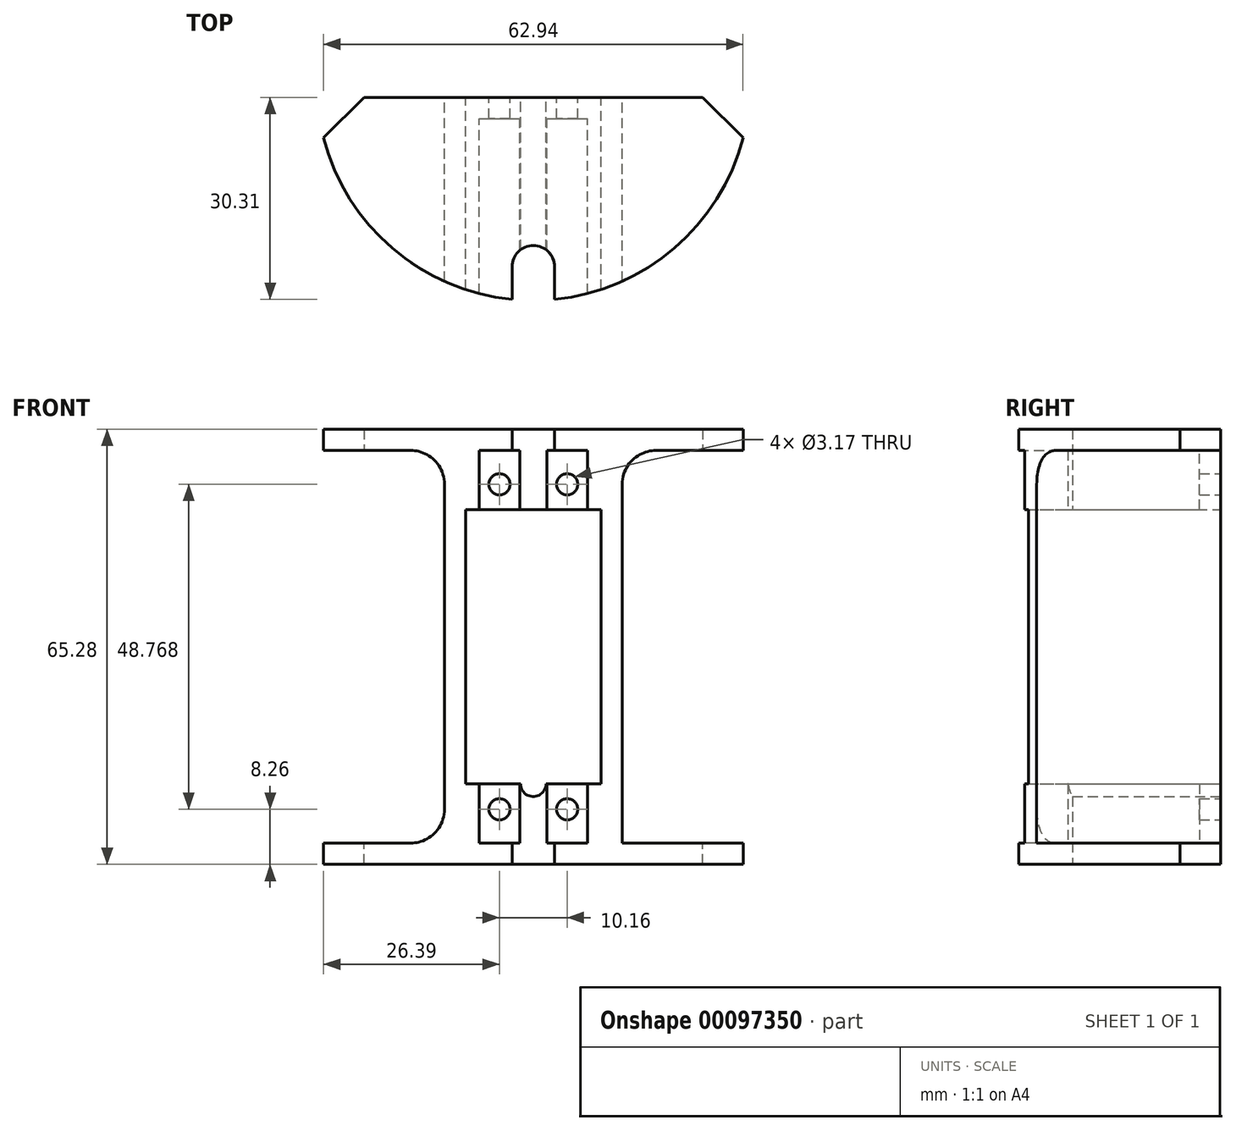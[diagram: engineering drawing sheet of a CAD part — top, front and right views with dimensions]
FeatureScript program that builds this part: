
annotation { "Feature Type Name" : "Feature", "Feature Type Description" : "" }
export const myFeature = defineFeature(function(context is Context, id is Id, definition is map)
    precondition{}
    {
        {
            var Q0;
            Q0=qCreatedBy(makeId("Front.planeOp"),FACE);
            var sketch = newSketch(context, id + "F0", { "sketchPlane" : qUnion([Q0])});
            skLineSegment(sketch, "E0", {"start": v(0, 0) * mm, "end": v(0, 41.15) * mm});
            skLineSegment(sketch, "E1", {"start": v(0, 41.15) * mm, "end": v(-20.32, 41.15) * mm});
            skLineSegment(sketch, "E2", {"start": v(-20.32, 41.15) * mm, "end": v(-20.32, 0) * mm});
            skLineSegment(sketch, "E3", {"start": v(-20.32, 0) * mm, "end": v(-12.07, 0) * mm});
            skLineSegment(sketch, "E4.0", {"start": v(-23.5, 50.04) * mm, "end": v(-23.5, -8.9) * mm});
            skLineSegment(sketch, "E5.0", {"start": v(3.17, 50.04) * mm, "end": v(-23.5, 50.04) * mm});
            skLineSegment(sketch, "E6.0", {"start": v(3.18, -8.9) * mm, "end": v(3.18, 50.04) * mm});
            skLineSegment(sketch, "E7.0", {"start": v(-23.5, -8.9) * mm, "end": v(3.18, -8.9) * mm});
            skLineSegment(sketch, "E8", {"start": v(-23.5, 44.96) * mm, "end": v(3.18, 44.96) * mm, "construction": true});
            skLineSegment(sketch, "E9", {"start": v(-23.5, 20.57) * mm, "end": v(3.18, 20.57) * mm, "construction": true});
            skLineSegment(sketch, "E10", {"start": v(-10.16, 50.04) * mm, "end": v(-10.16, -8.9) * mm, "construction": true});
            skLineSegment(sketch, "E11.MirrorCS", {"start": v(-23.5, -3.81) * mm, "end": v(3.18, -3.8) * mm, "construction": true});
            skCircle(sketch, "E12", {"center": v(-5.08, 44.96) * mm, "radius": 1.59 * mm});
            skCircle(sketch, "E13.MirrorC", {"center": v(-15.24, 44.96) * mm, "radius": 1.59 * mm});
            skCircle(sketch, "E14.MirrorC", {"center": v(-15.24, -3.81) * mm, "radius": 1.59 * mm});
            skCircle(sketch, "E15.MirrorC", {"center": v(-5.08, -3.81) * mm, "radius": 1.59 * mm});
            skArc(sketch, "E16", {"start": v(-12.07, 0) * mm, "mid": v(-10.16, -1.9) * mm, "end": v(-8.26, 0) * mm});
            skLineSegment(sketch, "E17.trimOffspring", {"start": v(-8.26, 0) * mm, "end": v(0, 0) * mm});
            skSolve(sketch);
        }
        {
            var Q0;
            Q0=makeQuery(id+"F0.imprint","IMPRINT",FACE,{"disambiguationData":[TD([[makeQuery(id+"F0.imprint","IMPRINT",EDGE,{"derivedFrom":sQuery(id+"F0.wireOp",EDGE,"E0")}),-1.0]])]});
            extrude(context, id + "F1", {"entities" : qUnion([Q0]), "depth" : 3.17 * mm});
        }
        {
            var Q0;
            Q0=makeQuery(id+"F1.opExtrude","CAP_FACE",FACE,{"disambiguationData":[OSD([sQuery(id+"F0.wireOp",EDGE,"E0"),sQuery(id+"F0.wireOp",EDGE,"E1"),sQuery(id+"F0.wireOp",EDGE,"E2"),sQuery(id+"F0.wireOp",EDGE,"E3"),sQuery(id+"F0.wireOp",EDGE,"E4.0"),sQuery(id+"F0.wireOp",EDGE,"E5.0"),sQuery(id+"F0.wireOp",EDGE,"E6.0"),sQuery(id+"F0.wireOp",EDGE,"E7.0"),sQuery(id+"F0.wireOp",EDGE,"E12"),sQuery(id+"F0.wireOp",EDGE,"E13.MirrorC"),sQuery(id+"F0.wireOp",EDGE,"E14.MirrorC"),sQuery(id+"F0.wireOp",EDGE,"E15.MirrorC")])],"isStart":false});
            var sketch = newSketch(context, id + "F2", { "sketchPlane" : qUnion([Q0])});
            skLineSegment(sketch, "E18", {"start": v(-2.03, 0) * mm, "end": v(-2.03, -8.9) * mm});
            skLineSegment(sketch, "E19", {"start": v(-2.03, 41.15) * mm, "end": v(-2.03, 50.04) * mm});
            skLineSegment(sketch, "E20", {"start": v(-10.16, -8.9) * mm, "end": v(-10.16, 50.04) * mm, "construction": true});
            skLineSegment(sketch, "E21.MirrorCS", {"start": v(-18.29, 0) * mm, "end": v(-18.29, -8.9) * mm});
            skLineSegment(sketch, "E22.MirrorCS", {"start": v(-18.29, 41.15) * mm, "end": v(-18.29, 50.04) * mm});
            skLineSegment(sketch, "E23", {"start": v(-8.13, 0) * mm, "end": v(-8.13, -8.9) * mm});
            skLineSegment(sketch, "E24", {"start": v(-8.13, 41.15) * mm, "end": v(-8.13, 50.04) * mm});
            skLineSegment(sketch, "E25.MirrorCS", {"start": v(-12.2, 0) * mm, "end": v(-12.2, -8.9) * mm});
            skLineSegment(sketch, "E26.MirrorCS", {"start": v(-12.2, 41.15) * mm, "end": v(-12.2, 50.04) * mm});
            skSolve(sketch);
        }
        {
            var Q0;
            {var subQ5=sQuery(id+"F2.wireOp",EDGE,"E18");Q0=makeQuery(id+"F2.imprint","IMPRINT",FACE,{"disambiguationData":[TD([[makeQuery(id+"F2.imprint","IMPRINT",EDGE,{"derivedFrom":subQ5}),1.0]])]});}
            var Q1;
            {var subQ0=sQuery(id+"F2.wireOp",EDGE,"E23");Q1=makeQuery(id+"F2.imprint","IMPRINT",FACE,{"disambiguationData":[TD([[makeQuery(id+"F2.imprint","IMPRINT",EDGE,{"derivedFrom":subQ0}),-1.0]])]});}
            var Q2;
            {var subQ2=sQuery(id+"F2.wireOp",EDGE,"E21.MirrorCS");Q2=makeQuery(id+"F2.imprint","IMPRINT",FACE,{"disambiguationData":[TD([[makeQuery(id+"F2.imprint","IMPRINT",EDGE,{"derivedFrom":subQ2}),-1.0]])]});}
            var Q3;
            {var subQ0=sQuery(id+"F2.wireOp",EDGE,"E24");Q3=makeQuery(id+"F2.imprint","IMPRINT",FACE,{"disambiguationData":[TD([[makeQuery(id+"F2.imprint","IMPRINT",EDGE,{"derivedFrom":subQ0}),1.0]])]});}
            extrude(context, id + "F3", {"entities" : qUnion([Q0, Q1, Q2, Q3]), "operationType" : NewBodyOperationType.ADD, "depth" : 38.1 * mm});
        }
        {
            var Q0;
            {var subQ0=sQuery(id+"F0.wireOp",EDGE,"E5.0");var subQ1=makeQuery(id+"F1.opExtrude","CAP_EDGE",EDGE,{"disambiguationData":[OSD([subQ0])],"isStart":false});Q0=makeQuery(id+"F3.boolean.opBoolean","MERGE",FACE,{"derivedFrom":[makeQuery(id+"F1.opExtrude","SWEPT_FACE",FACE,{"disambiguationData":[OSD([subQ0])]}),makeQuery(id+"F3.opExtrude","SWEPT_FACE",FACE,{"disambiguationData":[OSD([subQ0]),TDD([makeQuery(id+"F2.imprint","IMPRINT",EDGE,{"disambiguationData":[TD([[makeQuery(id+"F2.imprint","INTERSECT",VERTEX,{"derivedFrom":[makeQuery(id+"F1.opExtrude","CAP_EDGE",EDGE,{"disambiguationData":[OSD([sQuery(id+"F0.wireOp",EDGE,"E4.0")])],"isStart":false}),subQ1]}),1.0]])],"derivedFrom":subQ1})])]}),makeQuery(id+"F3.opExtrude","SWEPT_FACE",FACE,{"disambiguationData":[OSD([subQ0]),TDD([makeQuery(id+"F2.imprint","IMPRINT",EDGE,{"disambiguationData":[TD([[makeQuery(id+"F2.imprint","INTERSECT",VERTEX,{"derivedFrom":[subQ1,makeQuery(id+"F1.opExtrude","CAP_EDGE",EDGE,{"disambiguationData":[OSD([sQuery(id+"F0.wireOp",EDGE,"E6.0")])],"isStart":false})]}),-1.0]])],"derivedFrom":subQ1})])]}),makeQuery(id+"F3.opExtrude","SWEPT_FACE",FACE,{"disambiguationData":[OSD([subQ0]),TDD([makeQuery(id+"F2.imprint","IMPRINT",EDGE,{"disambiguationData":[TD([[makeQuery(id+"F2.imprint","INTERSECT",VERTEX,{"derivedFrom":[subQ1,sQuery(id+"F2.wireOp",EDGE,"E24")]}),-1.0]])],"derivedFrom":subQ1})])]})]});}
            var sketch = newSketch(context, id + "F4", { "sketchPlane" : qUnion([Q0])});
            skLineSegment(sketch, "E27", {"start": v(-10.16, 0) * mm, "end": v(-10.16, 2.03) * mm});
            skCircle(sketch, "E28", {"center": v(-10.16, 2.03) * mm, "radius": 32.5 * mm});
            skSolve(sketch);
        }
        {
            var Q0;
            {var subQ1=sQuery(id+"F0.wireOp",EDGE,"E5.0");var subQ3=makeQuery(id+"F1.opExtrude","CAP_EDGE",EDGE,{"disambiguationData":[OSD([subQ1])],"isStart":true});var subQ5=makeQuery(id+"F4.imprint","IMPRINT",VERTEX,{"derivedFrom":subQ3});Q0=makeQuery(id+"F4.imprint","IMPRINT",FACE,{"disambiguationData":[TD([[makeQuery(id+"F4.imprint","IMPRINT",EDGE,{"disambiguationData":[TD([[subQ5,-1.0]])],"derivedFrom":subQ3}),-1.0]])]});}
            var Q1;
            {var subQ2=sQuery(id+"F0.wireOp",EDGE,"E5.0");var subQ11=sQuery(id+"F2.wireOp",EDGE,"E26.MirrorCS");var subQ15=sQuery(id+"F4.wireOp",EDGE,"E28");var subQ24=makeQuery(id+"F3.opExtrude","SWEPT_EDGE",EDGE,{"disambiguationData":[OSD([subQ2,subQ11])]});var subQ25=makeQuery(id+"F4.imprint","INTERSECT",VERTEX,{"derivedFrom":[subQ24,subQ15]});Q1=makeQuery(id+"F4.imprint","IMPRINT",FACE,{"disambiguationData":[TD([[makeQuery(id+"F4.imprint","IMPRINT",EDGE,{"disambiguationData":[TD([[subQ25,-1.0]])],"derivedFrom":subQ15}),1.0]])]});}
            extrude(context, id + "F5", {"entities" : qUnion([Q0, Q1]), "operationType" : NewBodyOperationType.INTERSECT, "oppositeDirection" : true, "depth" : 101.6 * mm});
        }
        {
            var Q0;
            {var subQ0=sQuery(id+"F0.wireOp",EDGE,"E7.0");var subQ1=makeQuery(id+"F1.opExtrude","CAP_EDGE",EDGE,{"disambiguationData":[OSD([subQ0])],"isStart":false});Q0=makeQuery(id+"F3.boolean.opBoolean","MERGE",FACE,{"derivedFrom":[makeQuery(id+"F1.opExtrude","SWEPT_FACE",FACE,{"disambiguationData":[OSD([subQ0])]}),makeQuery(id+"F3.opExtrude","SWEPT_FACE",FACE,{"disambiguationData":[OSD([subQ0]),TDD([makeQuery(id+"F2.imprint","IMPRINT",EDGE,{"disambiguationData":[TD([[makeQuery(id+"F2.imprint","INTERSECT",VERTEX,{"derivedFrom":[makeQuery(id+"F1.opExtrude","CAP_EDGE",EDGE,{"disambiguationData":[OSD([sQuery(id+"F0.wireOp",EDGE,"E4.0")])],"isStart":false}),subQ1]}),-1.0]])],"derivedFrom":subQ1})])]}),makeQuery(id+"F3.opExtrude","SWEPT_FACE",FACE,{"disambiguationData":[OSD([subQ0]),TDD([makeQuery(id+"F2.imprint","IMPRINT",EDGE,{"disambiguationData":[TD([[makeQuery(id+"F2.imprint","INTERSECT",VERTEX,{"derivedFrom":[makeQuery(id+"F1.opExtrude","CAP_EDGE",EDGE,{"disambiguationData":[OSD([sQuery(id+"F0.wireOp",EDGE,"E6.0")])],"isStart":false}),subQ1]}),1.0]])],"derivedFrom":subQ1})])]}),makeQuery(id+"F3.opExtrude","SWEPT_FACE",FACE,{"disambiguationData":[OSD([subQ0]),TDD([makeQuery(id+"F2.imprint","IMPRINT",EDGE,{"disambiguationData":[TD([[makeQuery(id+"F2.imprint","INTERSECT",VERTEX,{"derivedFrom":[subQ1,sQuery(id+"F2.wireOp",EDGE,"E23")]}),1.0]])],"derivedFrom":subQ1})])]})]});}
            var sketch = newSketch(context, id + "F6", { "sketchPlane" : qUnion([Q0])});
            skLineSegment(sketch, "E29", {"start": v(-10.16, 0) * mm, "end": v(-10.16, -2.03) * mm});
            skArc(sketch, "E30", {"start": v(21.31, 6.07) * mm, "mid": v(-10.16, 30.47) * mm, "end": v(-41.63, 6.07) * mm});
            skLineSegment(sketch, "E31", {"start": v(-23.5, 0) * mm, "end": v(-35.56, 0) * mm});
            skLineSegment(sketch, "E32", {"start": v(3.18, 0) * mm, "end": v(15.24, 0) * mm});
            skLineSegment(sketch, "E33", {"start": v(-35.56, 0) * mm, "end": v(-41.63, 6.07) * mm});
            skLineSegment(sketch, "E34.MirrorCS", {"start": v(15.24, 0) * mm, "end": v(21.31, 6.07) * mm});
            skSolve(sketch);
        }
        {
            var Q0;
            Q0=makeQuery(id+"F6.imprint","IMPRINT",FACE,{"disambiguationData":[TD([[makeQuery(id+"F6.imprint","IMPRINT",EDGE,{"derivedFrom":sQuery(id+"F6.wireOp",EDGE,"E32")}),1.0]])]});
            var Q1;
            {var subQ1=sQuery(id+"F2.wireOp",EDGE,"E18");var subQ2=sQuery(id+"F0.wireOp",EDGE,"E7.0");var subQ3=makeQuery(id+"F3.opExtrude","SWEPT_EDGE",EDGE,{"disambiguationData":[OSD([subQ2,subQ1])]});Q1=makeQuery(id+"F6.imprint","IMPRINT",FACE,{"disambiguationData":[TD([[makeQuery(id+"F6.imprint","IMPRINT",EDGE,{"derivedFrom":subQ3}),-1.0]])]});}
            var Q2;
            {var subQ1=sQuery(id+"F2.wireOp",EDGE,"E21.MirrorCS");var subQ2=sQuery(id+"F0.wireOp",EDGE,"E7.0");var subQ3=makeQuery(id+"F3.opExtrude","SWEPT_EDGE",EDGE,{"disambiguationData":[OSD([subQ2,subQ1])]});Q2=makeQuery(id+"F6.imprint","IMPRINT",FACE,{"disambiguationData":[TD([[makeQuery(id+"F6.imprint","IMPRINT",EDGE,{"derivedFrom":subQ3}),1.0]])]});}
            var Q3;
            Q3=makeQuery(id+"F6.imprint","IMPRINT",FACE,{"disambiguationData":[TD([[makeQuery(id+"F6.imprint","IMPRINT",EDGE,{"derivedFrom":sQuery(id+"F6.wireOp",EDGE,"E31")}),-1.0]])]});
            var Q4;
            {var subQ0=sQuery(id+"F2.wireOp",EDGE,"E18");var subQ1=sQuery(id+"F0.wireOp",EDGE,"E7.0");var subQ2=makeQuery(id+"F3.opExtrude","SWEPT_EDGE",EDGE,{"disambiguationData":[OSD([subQ1,subQ0])]});Q4=makeQuery(id+"F6.imprint","IMPRINT",FACE,{"disambiguationData":[TD([[makeQuery(id+"F6.imprint","IMPRINT",EDGE,{"derivedFrom":subQ2}),1.0]])]});}
            extrude(context, id + "F7", {"entities" : qUnion([Q0, Q1, Q2, Q3, Q4]), "operationType" : NewBodyOperationType.ADD, "depth" : 3.17 * mm});
        }
        {
            var Q0;
            {var subQ0=sQuery(id+"F0.wireOp",EDGE,"E5.0");var subQ1=makeQuery(id+"F1.opExtrude","CAP_EDGE",EDGE,{"disambiguationData":[OSD([subQ0])],"isStart":false});Q0=makeQuery(id+"F3.boolean.opBoolean","MERGE",FACE,{"derivedFrom":[makeQuery(id+"F1.opExtrude","SWEPT_FACE",FACE,{"disambiguationData":[OSD([subQ0])]}),makeQuery(id+"F3.opExtrude","SWEPT_FACE",FACE,{"disambiguationData":[OSD([subQ0]),TDD([makeQuery(id+"F2.imprint","IMPRINT",EDGE,{"disambiguationData":[TD([[makeQuery(id+"F2.imprint","INTERSECT",VERTEX,{"derivedFrom":[makeQuery(id+"F1.opExtrude","CAP_EDGE",EDGE,{"disambiguationData":[OSD([sQuery(id+"F0.wireOp",EDGE,"E4.0")])],"isStart":false}),subQ1]}),1.0]])],"derivedFrom":subQ1})])]}),makeQuery(id+"F3.opExtrude","SWEPT_FACE",FACE,{"disambiguationData":[OSD([subQ0]),TDD([makeQuery(id+"F2.imprint","IMPRINT",EDGE,{"disambiguationData":[TD([[makeQuery(id+"F2.imprint","INTERSECT",VERTEX,{"derivedFrom":[subQ1,makeQuery(id+"F1.opExtrude","CAP_EDGE",EDGE,{"disambiguationData":[OSD([sQuery(id+"F0.wireOp",EDGE,"E6.0")])],"isStart":false})]}),-1.0]])],"derivedFrom":subQ1})])]}),makeQuery(id+"F3.opExtrude","SWEPT_FACE",FACE,{"disambiguationData":[OSD([subQ0]),TDD([makeQuery(id+"F2.imprint","IMPRINT",EDGE,{"disambiguationData":[TD([[makeQuery(id+"F2.imprint","INTERSECT",VERTEX,{"derivedFrom":[subQ1,sQuery(id+"F2.wireOp",EDGE,"E24")]}),-1.0]])],"derivedFrom":subQ1})])]})]});}
            var sketch = newSketch(context, id + "F8", { "sketchPlane" : qUnion([Q0])});
            skLineSegment(sketch, "E35.0.0", {"start": v(3.18, 0) * mm, "end": v(3.18, -27.6) * mm});
            skArc(sketch, "E35.0.1", {"start": v(3.17, -27.6) * mm, "mid": v(14.7, -18.9) * mm, "end": v(21.31, -6.07) * mm});
            skLineSegment(sketch, "E35.0.2", {"start": v(21.31, -6.07) * mm, "end": v(15.24, 0) * mm});
            skLineSegment(sketch, "E35.0.3", {"start": v(15.24, 0) * mm, "end": v(3.18, 0) * mm});
            skArc(sketch, "E36.0.0", {"start": v(-41.63, -6.07) * mm, "mid": v(-35.02, -18.9) * mm, "end": v(-23.5, -27.6) * mm});
            skLineSegment(sketch, "E36.0.1", {"start": v(-23.5, -27.6) * mm, "end": v(-23.5, 0) * mm});
            skLineSegment(sketch, "E36.0.2", {"start": v(-23.5, 0) * mm, "end": v(-35.56, 0) * mm});
            skLineSegment(sketch, "E36.0.3", {"start": v(-35.56, 0) * mm, "end": v(-41.63, -6.07) * mm});
            skArc(sketch, "E37.0.0", {"start": v(-18.29, -29.44) * mm, "mid": v(-15.26, -30.06) * mm, "end": v(-12.2, -30.4) * mm});
            skLineSegment(sketch, "E37.0.1", {"start": v(-12.2, -30.4) * mm, "end": v(-12.2, -3.18) * mm});
            skLineSegment(sketch, "E37.0.2", {"start": v(-12.2, -3.18) * mm, "end": v(-18.29, -3.18) * mm});
            skLineSegment(sketch, "E37.0.3", {"start": v(-18.29, -3.18) * mm, "end": v(-18.29, -29.44) * mm});
            skArc(sketch, "E38.0.0", {"start": v(-8.13, -30.4) * mm, "mid": v(-5.06, -30.06) * mm, "end": v(-2.03, -29.44) * mm});
            skLineSegment(sketch, "E38.0.1", {"start": v(-2.03, -29.44) * mm, "end": v(-2.03, -3.18) * mm});
            skLineSegment(sketch, "E38.0.2", {"start": v(-2.03, -3.18) * mm, "end": v(-8.13, -3.18) * mm});
            skLineSegment(sketch, "E38.0.3", {"start": v(-8.13, -3.18) * mm, "end": v(-8.13, -30.4) * mm});
            skSolve(sketch);
        }
        {
            var Q0;
            Q0=makeQuery(id+"F8.imprint","IMPRINT",FACE,{"disambiguationData":[TD([[makeQuery(id+"F8.imprint","IMPRINT",EDGE,{"derivedFrom":sQuery(id+"F8.wireOp",EDGE,"E36.0.0")}),1.0]])]});
            var Q1;
            Q1=makeQuery(id+"F8.imprint","IMPRINT",FACE,{"disambiguationData":[TD([[makeQuery(id+"F8.imprint","IMPRINT",EDGE,{"derivedFrom":sQuery(id+"F8.wireOp",EDGE,"E35.0.0")}),1.0]])]});
            var Q2;
            Q2=makeQuery(id+"F8.imprint","IMPRINT",FACE,{"disambiguationData":[TD([[makeQuery(id+"F8.imprint","IMPRINT",EDGE,{"derivedFrom":sQuery(id+"F8.wireOp",EDGE,"E37.0.0")}),1.0]])]});
            var Q3;
            Q3=makeQuery(id+"F8.imprint","IMPRINT",FACE,{"disambiguationData":[TD([[makeQuery(id+"F8.imprint","IMPRINT",EDGE,{"derivedFrom":sQuery(id+"F8.wireOp",EDGE,"E38.0.0")}),1.0]])]});
            var Q4;
            Q4=makeQuery(id+"F8.imprint","IMPRINT",FACE,{"disambiguationData":[TD([[makeQuery(id+"F8.imprint","IMPRINT",EDGE,{"derivedFrom":sQuery(id+"F8.wireOp",EDGE,"E35.0.0")}),-1.0]])]});
            extrude(context, id + "F9", {"entities" : qUnion([Q0, Q1, Q2, Q3, Q4]), "operationType" : NewBodyOperationType.ADD, "depth" : 3.17 * mm});
        }
        {
            var Q0;
            Q0=makeQuery(id+"F7.opExtrude","CAP_FACE",FACE,{"disambiguationData":[OSD([sQuery(id+"F0.wireOp",EDGE,"E7.0"),sQuery(id+"F6.wireOp",EDGE,"E30"),sQuery(id+"F6.wireOp",EDGE,"E31"),sQuery(id+"F6.wireOp",EDGE,"E32"),sQuery(id+"F6.wireOp",EDGE,"E33"),sQuery(id+"F6.wireOp",EDGE,"E34.MirrorCS")])],"isStart":false});
            var sketch = newSketch(context, id + "F10", { "sketchPlane" : qUnion([Q0])});
            skLineSegment(sketch, "E39", {"start": v(-10.16, 0) * mm, "end": v(-10.16, 25.4) * mm, "construction": true});
            skArc(sketch, "E40", {"start": v(-13.33, 25.4) * mm, "mid": v(-10.16, 22.23) * mm, "end": v(-6.98, 25.4) * mm});
            skLineSegment(sketch, "E41", {"start": v(-6.98, 25.4) * mm, "end": v(-6.98, 30.31) * mm});
            skLineSegment(sketch, "E42", {"start": v(-13.33, 25.4) * mm, "end": v(-13.33, 30.31) * mm});
            skArc(sketch, "E43.0", {"start": v(21.31, 6.07) * mm, "mid": v(10.98, 22.65) * mm, "end": v(-6.99, 30.31) * mm});
            skArc(sketch, "E44.trimOffspring", {"start": v(-13.33, 30.31) * mm, "mid": v(-31.3, 22.65) * mm, "end": v(-41.63, 6.07) * mm});
            skSolve(sketch);
        }
        {
            var Q0;
            Q0=makeQuery(id+"F10.imprint","IMPRINT",FACE,{"disambiguationData":[TD([[makeQuery(id+"F10.imprint","IMPRINT",EDGE,{"derivedFrom":sQuery(id+"F10.wireOp",EDGE,"E40")}),1.0]])]});
            extrude(context, id + "F11", {"entities" : qUnion([Q0]), "operationType" : NewBodyOperationType.REMOVE, "oppositeDirection" : true, "depth" : 127 * mm});
        }
        {
            var Q0;
            {var subQ0=sQuery(id+"F0.wireOp",EDGE,"E7.0");var subQ1=sQuery(id+"F0.wireOp",EDGE,"E4.0");Q0=makeQuery(id+"F3.boolean.opBoolean","MERGE",EDGE,{"derivedFrom":[makeQuery(id+"F1.opExtrude","SWEPT_EDGE",EDGE,{"disambiguationData":[OSD([subQ1,subQ0])]}),makeQuery(id+"F3.opExtrude","SWEPT_EDGE",EDGE,{"disambiguationData":[OSD([subQ1,subQ0])]})]});}
            var Q1;
            {var subQ0=sQuery(id+"F0.wireOp",EDGE,"E5.0");var subQ1=sQuery(id+"F0.wireOp",EDGE,"E4.0");Q1=makeQuery(id+"F3.boolean.opBoolean","MERGE",EDGE,{"derivedFrom":[makeQuery(id+"F1.opExtrude","SWEPT_EDGE",EDGE,{"disambiguationData":[OSD([subQ1,subQ0])]}),makeQuery(id+"F3.opExtrude","SWEPT_EDGE",EDGE,{"disambiguationData":[OSD([subQ1,subQ0])]})]});}
            var Q2;
            {var subQ0=sQuery(id+"F0.wireOp",EDGE,"E6.0");var subQ1=sQuery(id+"F0.wireOp",EDGE,"E5.0");Q2=makeQuery(id+"F3.boolean.opBoolean","MERGE",EDGE,{"derivedFrom":[makeQuery(id+"F1.opExtrude","SWEPT_EDGE",EDGE,{"disambiguationData":[OSD([subQ1,subQ0])]}),makeQuery(id+"F3.opExtrude","SWEPT_EDGE",EDGE,{"disambiguationData":[OSD([subQ1,subQ0])]})]});}
            var Q3;
            {var subQ0=sQuery(id+"F0.wireOp",EDGE,"E7.0");var subQ1=sQuery(id+"F0.wireOp",EDGE,"E6.0");Q3=makeQuery(id+"F3.boolean.opBoolean","MERGE",EDGE,{"derivedFrom":[makeQuery(id+"F1.opExtrude","SWEPT_EDGE",EDGE,{"disambiguationData":[OSD([subQ1,subQ0])]}),makeQuery(id+"F3.opExtrude","SWEPT_EDGE",EDGE,{"disambiguationData":[OSD([subQ1,subQ0])]})]});}
            fillet(context, id + "F12", {"entities" : qUnion([Q0, Q1, Q2, Q3]), "radius" : 5.08 * mm, "tangentPropagation" : true, "allowEdgeOverflow" : false});
        }
    });
